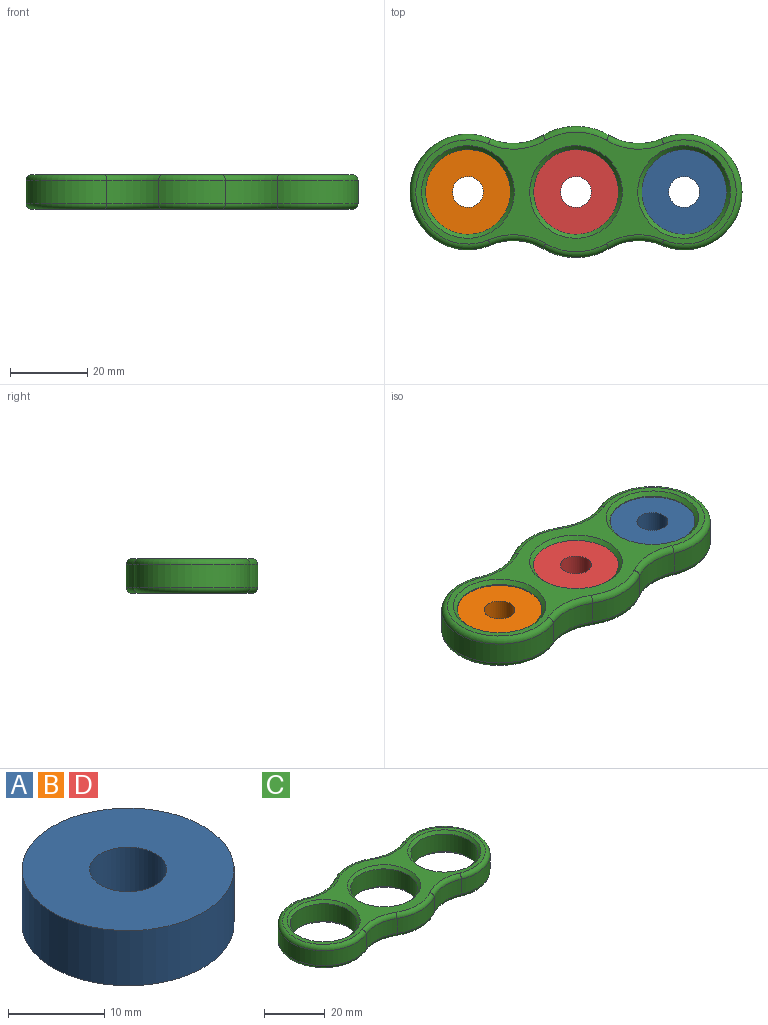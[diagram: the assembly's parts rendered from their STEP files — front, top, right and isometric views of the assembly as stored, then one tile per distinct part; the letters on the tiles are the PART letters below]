
ASSEMBLY  parts=4 mates=3
PART A: 4 faces, bbox 22x22x7 mm
  f0: cylinder r=4mm len=8mm, axis (0,0,-1), area 175.9mm2, adj f2,f3
  f1: cylinder r=11mm len=22mm, axis (0,0,-1), area 483.8mm2, adj f2,f3
  f2: plane 22x22mm, normal (0,0,1), area 329.9mm2, adj f0,f1
  f3: plane 22x22mm, normal (0,0,-1), area 329.9mm2, adj f0,f1
PART B: same geometry as A
PART C: 35 faces, bbox 88.5x36.8x9 mm
  f0: cylinder r=15mm len=30mm, axis (0,0,-1), area 355.4mm2, adj f1,f10,f17,f25
  f1: cylinder r=15mm len=13.49mm, axis (0,0,-1), area 84.2mm2, adj f0,f2,f15,f23
  f2: cylinder r=17mm len=17.23mm, axis (0,0,-1), area 108.4mm2, adj f1,f3,f13,f21
  f3: cylinder r=15mm len=13.49mm, axis (0,0,-1), area 84.2mm2, adj f2,f4,f14,f22
  f4: cylinder r=15mm len=30mm, axis (0,0,-1), area 355.4mm2, adj f3,f5,f16,f24
  f5: cylinder r=15mm len=13.49mm, axis (0,0,-1), area 84.2mm2, adj f4,f6,f18,f26
  f6: cylinder r=17mm len=17.23mm, axis (0,0,-1), area 108.4mm2, adj f5,f10,f20,f28
  f7: cylinder r=11mm len=22mm, axis (0,0,-1), area 483.8mm2, adj f31,f32
  f8: cylinder r=11mm len=22mm, axis (0,0,-1), area 483.8mm2, adj f29,f30
  f9: cylinder r=11mm len=22mm, axis (0,0,-1), area 483.8mm2, adj f33,f34
  f10: cylinder r=15mm len=13.49mm, axis (0,0,-1), area 84.2mm2, adj f0,f6,f19,f27
  f11: plane 83x31mm, normal (0,0,1), area 653.6mm2, adj f21,f22,f23,f24,f25,f26,f27,f28
  f12: plane 83x31mm, normal (0,0,-1), area 653.6mm2, adj f13,f14,f15,f16,f17,f18,f19,f20
  f13: torus R=15.5mm, axis (0,0,1), area 41.2mm2, adj f2,f12,f14,f15
  f14: torus R=16.5mm, axis (0,0,1), area 34.2mm2, adj f3,f12,f13,f16
  f15: torus R=16.5mm, axis (0,0,1), area 34.2mm2, adj f1,f12,f13,f17
  f16: torus R=13.5mm, axis (0,0,1), area 134.5mm2, adj f4,f12,f14,f18
  f17: torus R=13.5mm, axis (0,0,1), area 134.5mm2, adj f0,f12,f15,f19
  f18: torus R=16.5mm, axis (0,0,1), area 34.2mm2, adj f5,f12,f16,f20
  f19: torus R=16.5mm, axis (0,0,1), area 34.2mm2, adj f10,f12,f17,f20
  f20: torus R=15.5mm, axis (0,0,1), area 41.2mm2, adj f6,f12,f18,f19
  f21: torus R=15.5mm, axis (0,0,1), area 41.2mm2, adj f2,f11,f22,f23
  f22: torus R=16.5mm, axis (0,0,1), area 34.2mm2, adj f3,f11,f21,f24
  f23: torus R=16.5mm, axis (0,0,1), area 34.2mm2, adj f1,f11,f21,f25
  f24: torus R=13.5mm, axis (0,0,1), area 134.5mm2, adj f4,f11,f22,f26
  f25: torus R=13.5mm, axis (0,0,1), area 134.5mm2, adj f0,f11,f23,f27
  f26: torus R=16.5mm, axis (0,0,1), area 34.2mm2, adj f5,f11,f24,f28
  f27: torus R=16.5mm, axis (0,0,1), area 34.2mm2, adj f10,f11,f25,f28
  f28: torus R=15.5mm, axis (0,0,1), area 41.2mm2, adj f6,f11,f26,f27
  f29: cone r=11mm half-angle=45deg, axis (0,0,1), area 102.2mm2, adj f8,f11
  f30: cone r=12mm half-angle=45deg, axis (0,0,-1), area 102.2mm2, adj f8,f12
  f31: cone r=11mm half-angle=45deg, axis (0,0,1), area 102.2mm2, adj f7,f11
  f32: cone r=12mm half-angle=45deg, axis (0,0,-1), area 102.2mm2, adj f7,f12
  f33: cone r=11mm half-angle=45deg, axis (0,0,1), area 102.2mm2, adj f9,f11
  f34: cone r=12mm half-angle=45deg, axis (0,0,-1), area 102.2mm2, adj f9,f12
PART D: same geometry as A
PLACE A t=(25.94,-1.89,-3.13)mm
PLACE B t=(-30.06,-1.89,-3.19)mm
PLACE C t=(-2.06,-1.89,-3.93)mm
PLACE D t=(-2.06,-1.89,-2.93)mm
MATE cylindrical A.f0 <-> C.f0  axis (0,0,-1) through (25.94,-1.89,-3.13)mm
MATE cylindrical B.f0 <-> C.f4  axis (0,0,-1) through (-30.06,-1.89,0.31)mm
MATE cylindrical D.f0 <-> C.f2  axis (0,0,-1) through (-2.06,-1.89,0.57)mm
